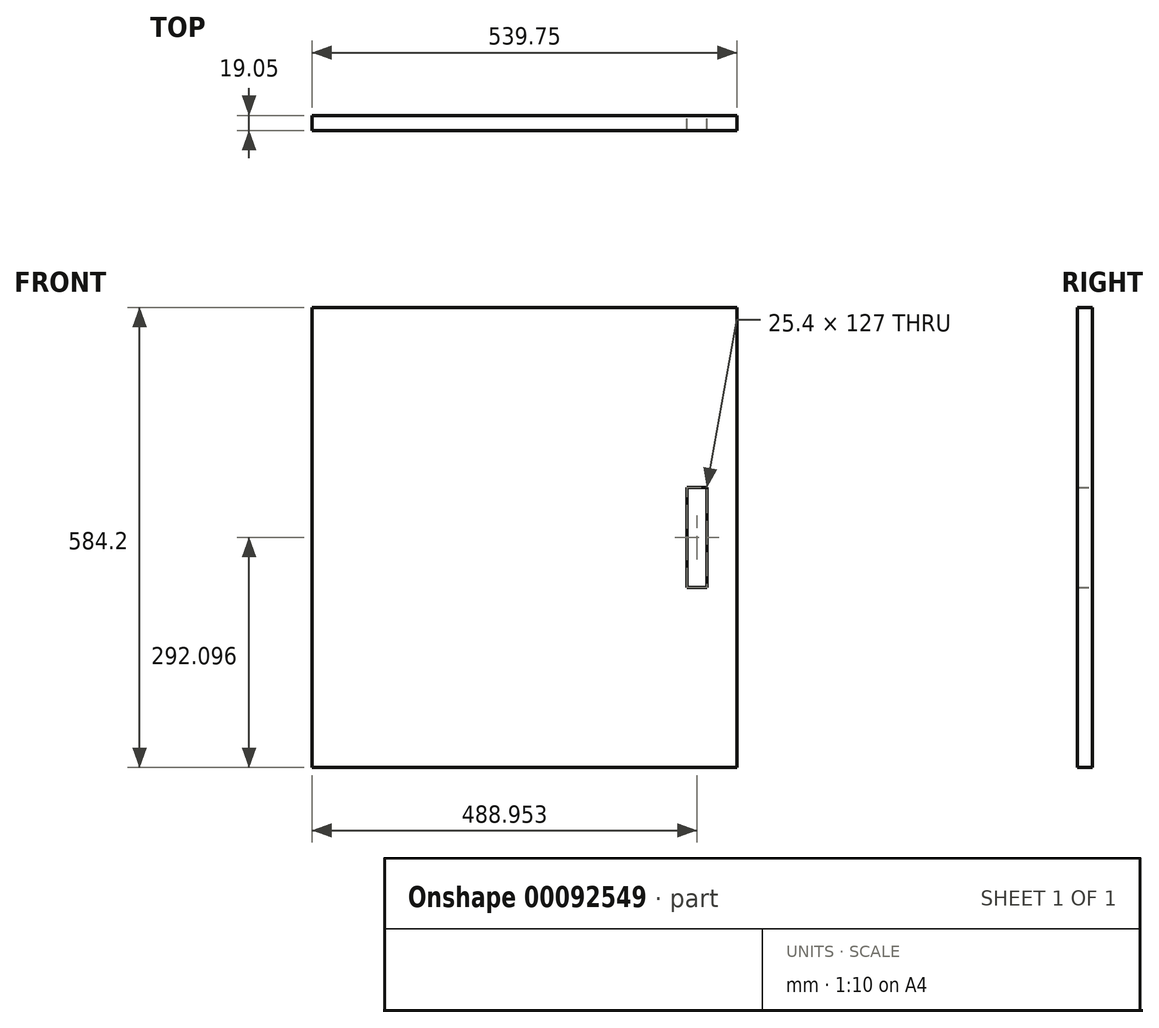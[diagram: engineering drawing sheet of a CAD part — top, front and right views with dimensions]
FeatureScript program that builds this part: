
annotation { "Feature Type Name" : "Feature", "Feature Type Description" : "" }
export const myFeature = defineFeature(function(context is Context, id is Id, definition is map)
    precondition{}
    {
        {
            var Q0;
            Q0=qCreatedBy(makeId("Front.planeOp"),FACE);
            var sketch = newSketch(context, id + "F0", { "sketchPlane" : qUnion([Q0])});
            skLineSegment(sketch, "E0.bottom", {"start": v(-298.8, 452.6) * mm, "end": v(240.95, 452.6) * mm});
            skLineSegment(sketch, "E0.top", {"start": v(-298.8, -131.6) * mm, "end": v(240.95, -131.6) * mm});
            skLineSegment(sketch, "E0.left", {"start": v(-298.8, 452.6) * mm, "end": v(-298.8, -131.6) * mm});
            skLineSegment(sketch, "E0.right", {"start": v(240.95, 452.6) * mm, "end": v(240.95, -131.6) * mm});
            skLineSegment(sketch, "E1.bottom", {"start": v(177.45, 224) * mm, "end": v(202.85, 224) * mm});
            skLineSegment(sketch, "E1.top", {"start": v(177.45, 97) * mm, "end": v(202.85, 97) * mm});
            skLineSegment(sketch, "E1.left", {"start": v(177.45, 224) * mm, "end": v(177.45, 97) * mm});
            skLineSegment(sketch, "E1.right", {"start": v(202.85, 224) * mm, "end": v(202.85, 97) * mm});
            skSolve(sketch);
        }
        {
            var Q0;
            Q0=makeQuery(id+"F0.imprint","IMPRINT",FACE,{"disambiguationData":[TD([[makeQuery(id+"F0.imprint","IMPRINT",EDGE,{"derivedFrom":sQuery(id+"F0.wireOp",EDGE,"E0.bottom")}),-1.0]])]});
            extrude(context, id + "F1", {"entities" : qUnion([Q0]), "depth" : 19.05 * mm});
        }
    });
